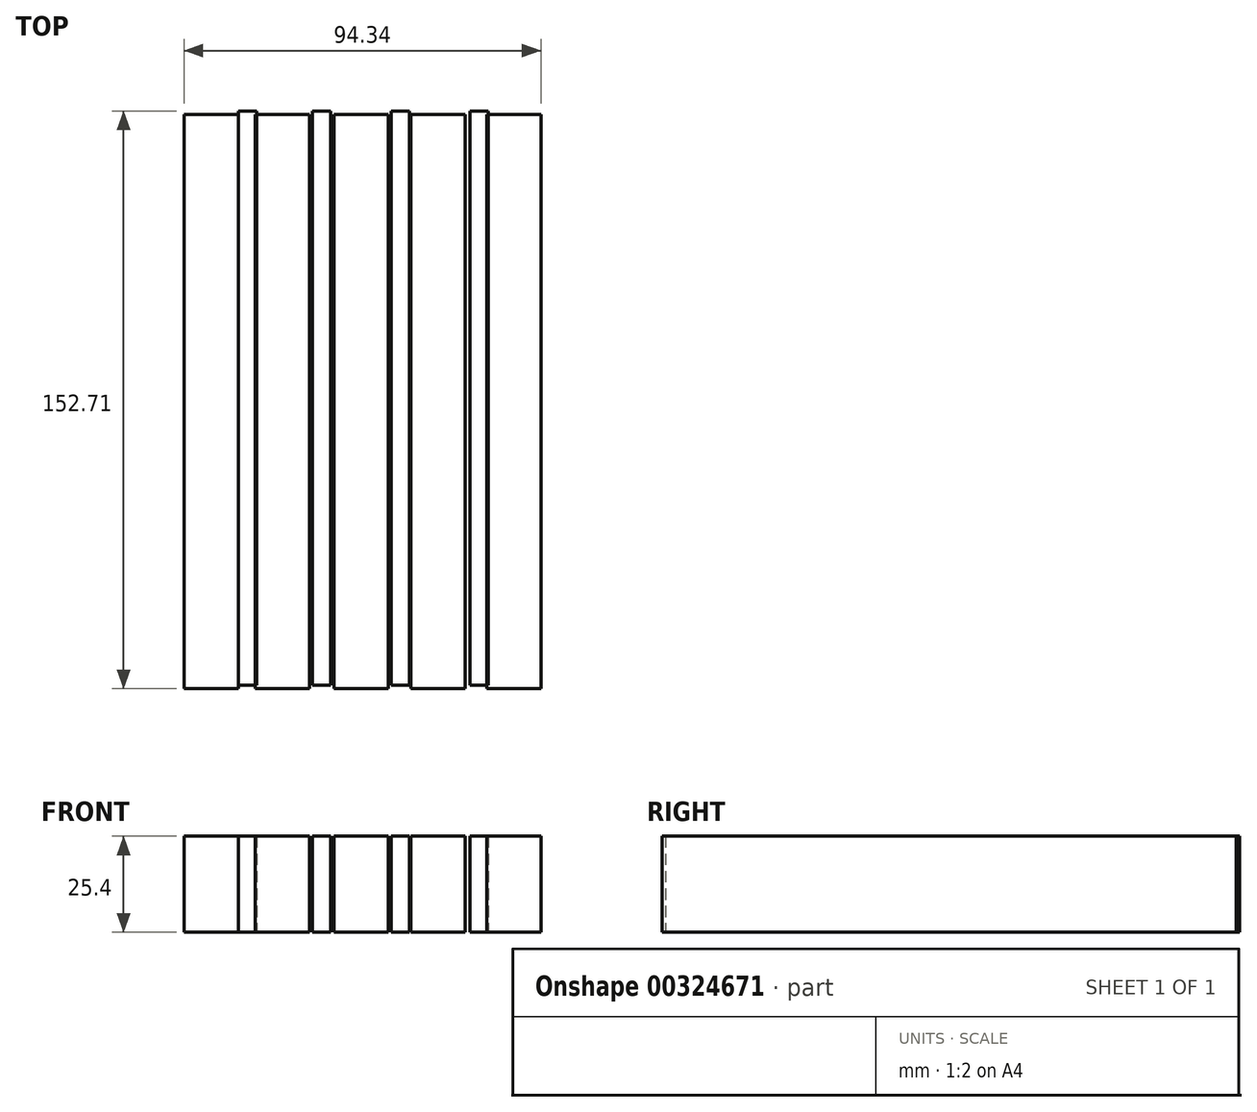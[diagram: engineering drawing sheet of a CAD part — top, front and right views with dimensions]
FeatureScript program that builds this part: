
annotation { "Feature Type Name" : "Feature", "Feature Type Description" : "" }
export const myFeature = defineFeature(function(context is Context, id is Id, definition is map)
    precondition{}
    {
        {
            var Q0;
            Q0=qCreatedBy(makeId("Top.planeOp"),FACE);
            var sketch = newSketch(context, id + "F0", { "sketchPlane" : qUnion([Q0])});
            skLineSegment(sketch, "E0.bottom", {"start": v(-75.9, 75.74) * mm, "end": v(-61.57, 75.74) * mm});
            skLineSegment(sketch, "E0.top", {"start": v(-75.9, -76.05) * mm, "end": v(-61.57, -76.05) * mm});
            skLineSegment(sketch, "E0.left", {"start": v(-75.9, 75.74) * mm, "end": v(-75.9, -76.05) * mm});
            skLineSegment(sketch, "E0.right", {"start": v(-61.57, 75.74) * mm, "end": v(-61.57, -76.05) * mm});
            skSolve(sketch);
        }
        {
            var Q0;
            Q0=makeQuery(id+"F0.imprint","IMPRINT",FACE,{"disambiguationData":[TD([[makeQuery(id+"F0.imprint","IMPRINT",EDGE,{"derivedFrom":sQuery(id+"F0.wireOp",EDGE,"E0.bottom")}),-1.0]])]});
            extrude(context, id + "F1", {"entities" : qUnion([Q0]), "depth" : 25.4 * mm});
        }
        {
            var Q0;
            Q0=makeQuery(id+"F1.opExtrude","SWEPT_BODY",BODY,{"disambiguationData":[OSD([sQuery(id+"F0.wireOp",EDGE,"E0.bottom"),sQuery(id+"F0.wireOp",EDGE,"E0.top"),sQuery(id+"F0.wireOp",EDGE,"E0.left"),sQuery(id+"F0.wireOp",EDGE,"E0.right")])]});
            transform(context, id + "F2", {"entities" : qUnion([Q0]), "transformType" : TransformType.TRANSLATION_3D, "dx" : 18.8 * mm, "dy" : 0 * mm, "dz" : 0 * mm, "makeCopy" : true});
        }
        {
            var Q0;
            Q0=makeQuery(id+"F2.opPattern","COPY",BODY,{"derivedFrom":makeQuery(id+"F1.opExtrude","SWEPT_BODY",BODY,{"disambiguationData":[OSD([sQuery(id+"F0.wireOp",EDGE,"E0.bottom"),sQuery(id+"F0.wireOp",EDGE,"E0.top"),sQuery(id+"F0.wireOp",EDGE,"E0.left"),sQuery(id+"F0.wireOp",EDGE,"E0.right")])]}),"instanceName":"1"});
            transform(context, id + "F3", {"entities" : qUnion([Q0]), "transformType" : TransformType.TRANSLATION_3D, "dx" : 20.83 * mm, "dy" : 0 * mm, "dz" : 0 * mm, "makeCopy" : true});
        }
        {
            var Q0;
            Q0=makeQuery(id+"F3.opPattern","COPY",BODY,{"derivedFrom":makeQuery(id+"F2.opPattern","COPY",BODY,{"derivedFrom":makeQuery(id+"F1.opExtrude","SWEPT_BODY",BODY,{"disambiguationData":[OSD([sQuery(id+"F0.wireOp",EDGE,"E0.bottom"),sQuery(id+"F0.wireOp",EDGE,"E0.top"),sQuery(id+"F0.wireOp",EDGE,"E0.left"),sQuery(id+"F0.wireOp",EDGE,"E0.right")])]}),"instanceName":"1"}),"instanceName":"1"});
            transform(context, id + "F4", {"entities" : qUnion([Q0]), "transformType" : TransformType.TRANSLATION_3D, "dx" : 20.32 * mm, "dy" : 0 * mm, "dz" : 0 * mm, "makeCopy" : true});
        }
        {
            var Q0;
            Q0=makeQuery(id+"F4.opPattern","COPY",BODY,{"derivedFrom":makeQuery(id+"F3.opPattern","COPY",BODY,{"derivedFrom":makeQuery(id+"F2.opPattern","COPY",BODY,{"derivedFrom":makeQuery(id+"F1.opExtrude","SWEPT_BODY",BODY,{"disambiguationData":[OSD([sQuery(id+"F0.wireOp",EDGE,"E0.bottom"),sQuery(id+"F0.wireOp",EDGE,"E0.top"),sQuery(id+"F0.wireOp",EDGE,"E0.left"),sQuery(id+"F0.wireOp",EDGE,"E0.right")])]}),"instanceName":"1"}),"instanceName":"1"}),"instanceName":"1"});
            transform(context, id + "F5", {"entities" : qUnion([Q0]), "transformType" : TransformType.TRANSLATION_3D, "dx" : 20.07 * mm, "dy" : 0 * mm, "dz" : 0 * mm, "makeCopy" : true});
        }
        {
            var Q0;
            Q0=qCreatedBy(makeId("Top.planeOp"),FACE);
            var sketch = newSketch(context, id + "F6", { "sketchPlane" : qUnion([Q0])});
            skLineSegment(sketch, "E1.bottom", {"start": v(-61.57, 76.66) * mm, "end": v(-56.7, 76.66) * mm});
            skLineSegment(sketch, "E1.top", {"start": v(-61.57, -75.13) * mm, "end": v(-56.7, -75.13) * mm});
            skLineSegment(sketch, "E1.left", {"start": v(-61.57, 76.66) * mm, "end": v(-61.57, -75.13) * mm});
            skLineSegment(sketch, "E1.right", {"start": v(-56.7, 76.66) * mm, "end": v(-56.7, -75.13) * mm});
            skLineSegment(sketch, "E2.bottom", {"start": v(-59.13, 16.92) * mm, "end": v(-59.13, 16.92) * mm});
            skLineSegment(sketch, "E2.top", {"start": v(-59.13, 73.91) * mm, "end": v(-59.13, 73.91) * mm});
            skLineSegment(sketch, "E2.left", {"start": v(-59.13, 16.92) * mm, "end": v(-59.13, 73.91) * mm});
            skLineSegment(sketch, "E2.right", {"start": v(-59.13, 16.92) * mm, "end": v(-59.13, 73.91) * mm});
            skPoint(sketch, "E3.oppositeSnap0", {"position": v(-59.13, 45.42) * mm});
            skLineSegment(sketch, "E3.bottom", {"start": v(-59.13, 73.91) * mm, "end": v(-56.7, 73.91) * mm});
            skLineSegment(sketch, "E3.top", {"start": v(-59.13, 45.42) * mm, "end": v(-56.7, 45.42) * mm});
            skLineSegment(sketch, "E3.left", {"start": v(-59.13, 73.91) * mm, "end": v(-59.13, 45.42) * mm});
            skLineSegment(sketch, "E3.right", {"start": v(-56.7, 73.91) * mm, "end": v(-56.7, 45.42) * mm});
            skSolve(sketch);
        }
        {
            var Q0;
            Q0 = qSketchRegion(id + "F6", true);
            extrude(context, id + "F7", {"entities" : qUnion([Q0]), "depth" : 25.4 * mm});
        }
        {
            var Q0;
            Q0=makeQuery(id+"F7.opExtrude","SWEPT_BODY",BODY,{"disambiguationData":[OSD([sQuery(id+"F6.wireOp",EDGE,"E1.bottom"),sQuery(id+"F6.wireOp",EDGE,"E1.top"),sQuery(id+"F6.wireOp",EDGE,"E1.left"),sQuery(id+"F6.wireOp",EDGE,"E1.right"),sQuery(id+"F6.wireOp",EDGE,"E3.right")])]});
            transform(context, id + "F8", {"entities" : qUnion([Q0]), "transformType" : TransformType.TRANSLATION_3D, "dx" : 19.56 * mm, "dy" : 0 * mm, "dz" : 0 * mm, "makeCopy" : true});
        }
        {
            var Q0;
            Q0=makeQuery(id+"F8.opPattern","COPY",BODY,{"derivedFrom":makeQuery(id+"F7.opExtrude","SWEPT_BODY",BODY,{"disambiguationData":[OSD([sQuery(id+"F6.wireOp",EDGE,"E1.bottom"),sQuery(id+"F6.wireOp",EDGE,"E1.top"),sQuery(id+"F6.wireOp",EDGE,"E1.left"),sQuery(id+"F6.wireOp",EDGE,"E1.right"),sQuery(id+"F6.wireOp",EDGE,"E3.right")])]}),"instanceName":"1"});
            transform(context, id + "F9", {"entities" : qUnion([Q0]), "transformType" : TransformType.TRANSLATION_3D, "dx" : 20.83 * mm, "dy" : 0 * mm, "dz" : 0 * mm, "makeCopy" : true});
        }
        {
            var Q0;
            Q0=makeQuery(id+"F9.opPattern","COPY",BODY,{"derivedFrom":makeQuery(id+"F8.opPattern","COPY",BODY,{"derivedFrom":makeQuery(id+"F7.opExtrude","SWEPT_BODY",BODY,{"disambiguationData":[OSD([sQuery(id+"F6.wireOp",EDGE,"E1.bottom"),sQuery(id+"F6.wireOp",EDGE,"E1.top"),sQuery(id+"F6.wireOp",EDGE,"E1.left"),sQuery(id+"F6.wireOp",EDGE,"E1.right"),sQuery(id+"F6.wireOp",EDGE,"E3.right")])]}),"instanceName":"1"}),"instanceName":"1"});
            transform(context, id + "F10", {"entities" : qUnion([Q0]), "transformType" : TransformType.TRANSLATION_3D, "dx" : 20.83 * mm, "dy" : 0 * mm, "dz" : 0 * mm, "makeCopy" : true});
        }
    });
